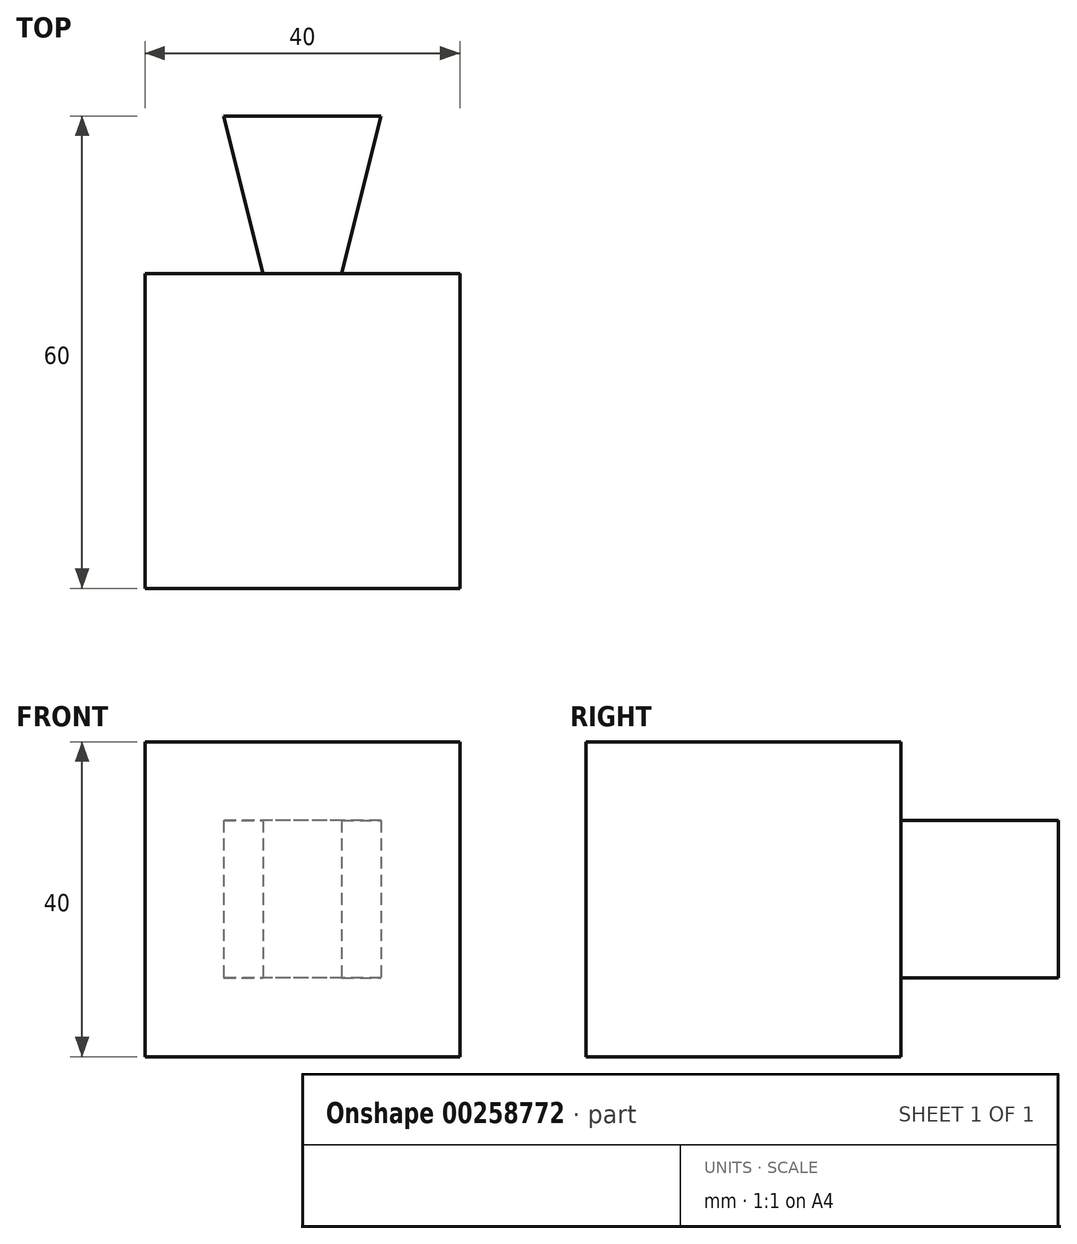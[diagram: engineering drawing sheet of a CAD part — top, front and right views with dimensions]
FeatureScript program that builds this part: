
annotation { "Feature Type Name" : "Feature", "Feature Type Description" : "" }
export const myFeature = defineFeature(function(context is Context, id is Id, definition is map)
    precondition{}
    {
        {
            var Q0;
            Q0=qCreatedBy(makeId("Front.planeOp"),FACE);
            var sketch = newSketch(context, id + "F0", { "sketchPlane" : qUnion([Q0])});
            skLineSegment(sketch, "E0.bottom", {"start": v(20, -20) * mm, "end": v(-20, -20) * mm});
            skLineSegment(sketch, "E0.top", {"start": v(20, 20) * mm, "end": v(-20, 20) * mm});
            skLineSegment(sketch, "E0.left", {"start": v(20, -20) * mm, "end": v(20, 20) * mm});
            skLineSegment(sketch, "E0.right", {"start": v(-20, -20) * mm, "end": v(-20, 20) * mm});
            skPoint(sketch, "E0.middle", {"position": v(0, 0) * mm});
            skSolve(sketch);
        }
        {
            var Q0;
            Q0=makeQuery(id+"F0.imprint","IMPRINT",FACE,{"disambiguationData":[TD([[makeQuery(id+"F0.imprint","IMPRINT",EDGE,{"derivedFrom":sQuery(id+"F0.wireOp",EDGE,"E0.bottom")}),-1.0]])]});
            extrude(context, id + "F1", {"entities" : qUnion([Q0]), "depth" : 40 * mm});
        }
        {
            var Q0;
            Q0=qCreatedBy(makeId("Top.planeOp"),FACE);
            var sketch = newSketch(context, id + "F2", { "sketchPlane" : qUnion([Q0])});
            skLineSegment(sketch, "E1", {"start": v(5, 0) * mm, "end": v(-5, 0) * mm});
            skLineSegment(sketch, "E2", {"start": v(10, 20) * mm, "end": v(-10, 20) * mm});
            skLineSegment(sketch, "E3", {"start": v(-10, 20) * mm, "end": v(-5, 0) * mm});
            skLineSegment(sketch, "E4", {"start": v(5, 0) * mm, "end": v(10, 20) * mm});
            skSolve(sketch);
        }
        {
            var Q0;
            Q0=makeQuery(id+"F2.imprint","IMPRINT",FACE,{"disambiguationData":[TD([[makeQuery(id+"F2.imprint","IMPRINT",EDGE,{"derivedFrom":sQuery(id+"F2.wireOp",EDGE,"E1")}),-1.0]])]});
            extrude(context, id + "F3", {"entities" : qUnion([Q0]), "operationType" : NewBodyOperationType.ADD, "endBound" : BoundingType.SYMMETRIC, "depth" : 20 * mm});
        }
    });
